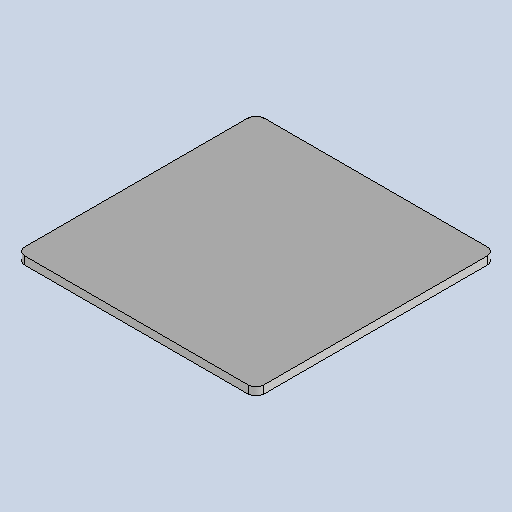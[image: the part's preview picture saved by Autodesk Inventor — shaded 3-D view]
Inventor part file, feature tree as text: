
AUTODESK INVENTOR PART (.ipt)
format: ipt  version: 2025.1 (Build 291241020, 241B)  size: 147,968 bytes
history: native  units: mm
features: other x2, sheet_metal_op x1, chamfer x1, sketch x1
ambient origin geometry x8: Origin, YZ Plane, XZ Plane, XY Plane, X Axis, Y Axis, Z Axis, Center Point
bodies: Body1 (feature_tree)
feature tree (5):
  sheet_metal_op  "Face3"
  chamfer  "Corner Round1"
  sketch  "Sketch1"  dims[d154=60.0mm d155=60.0mm d156=2.0mm d172=30.5mm d178=2.0mm]
  other  "Plate5"
  other  "Definition1"
